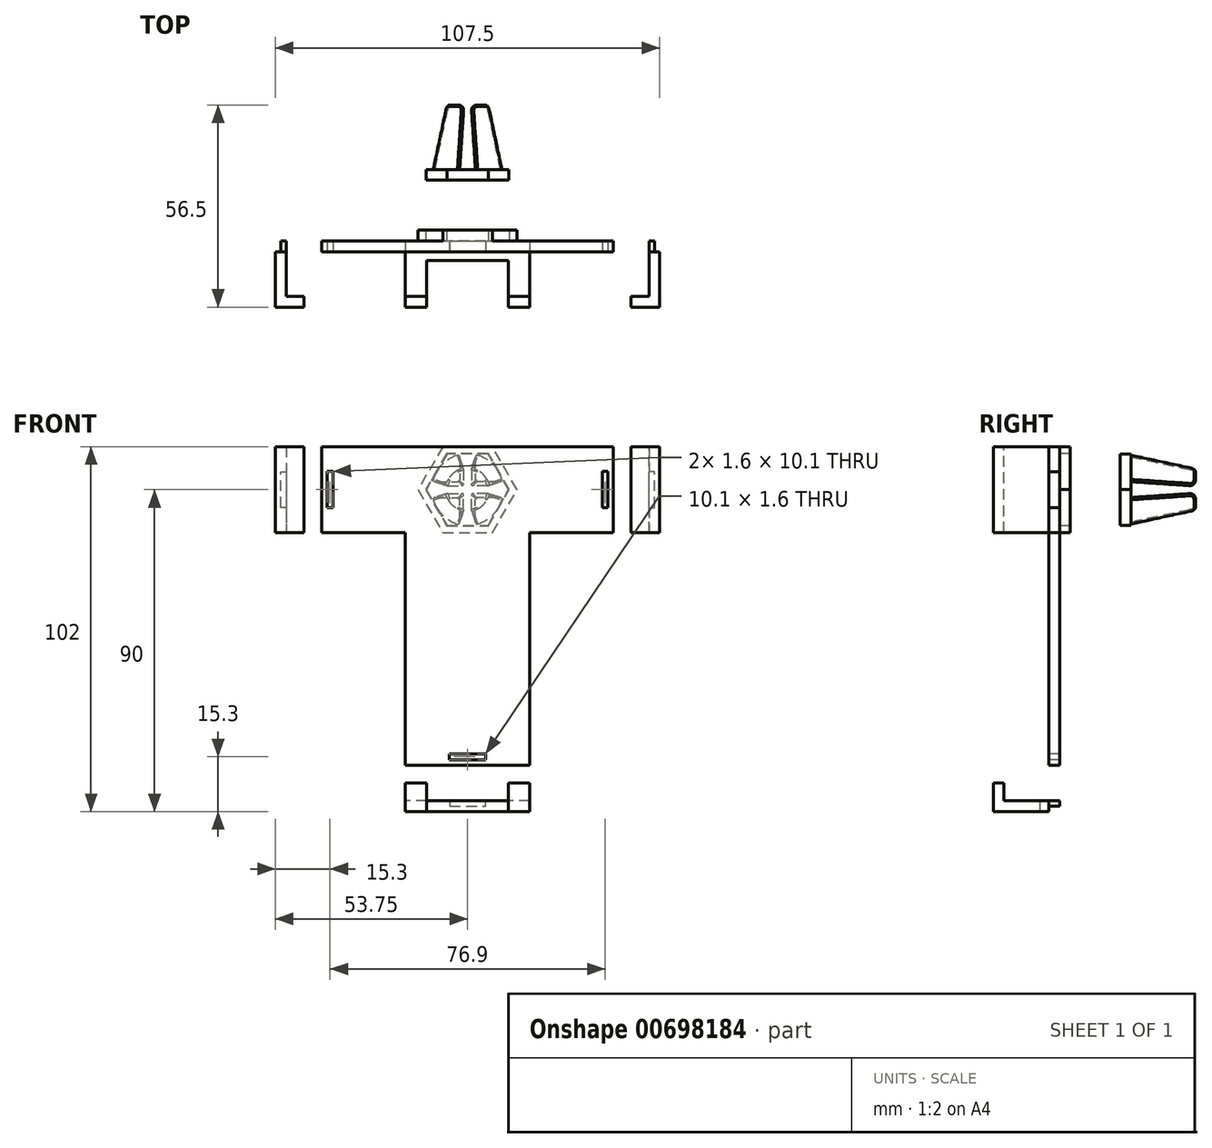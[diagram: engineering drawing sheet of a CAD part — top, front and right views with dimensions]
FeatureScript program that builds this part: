
annotation { "Feature Type Name" : "Feature", "Feature Type Description" : "" }
export const myFeature = defineFeature(function(context is Context, id is Id, definition is map)
    precondition{}
    {
        {
            assignVariable(context, id + "F0", {"name" : "depth_phone", "anyValue" : 12});
        }
        {
            var Q0;
            Q0=qCreatedBy(makeId("Front.planeOp"),FACE);
            var sketch = newSketch(context, id + "F1", { "sketchPlane" : qUnion([Q0])});
            skCircle(sketch, "E0", {"center": v(0, 0) * mm, "radius": 10 * mm});
            skSolve(sketch);
        }
        {
            var Q0;
            Q0=qSketchRegion(id+"F1",true);
            extrude(context, id + "F2", {"entities" : qUnion([Q0]), "oppositeDirection" : true, "depth" : 3 * mm});
        }
        {
            var Q0;
            Q0=makeQuery(id+"F2.opExtrude","CAP_FACE",FACE,{"disambiguationData":[OSD([sQuery(id+"F1.wireOp",EDGE,"E0")])],"isStart":false});
            var sketch = newSketch(context, id + "F3", { "sketchPlane" : qUnion([Q0])});
            skLineSegment(sketch, "E1.top", {"start": v(-9.75, 2.2) * mm, "end": v(-2.2, 2.2) * mm});
            skLineSegment(sketch, "E1.right", {"start": v(-2.2, 9.75) * mm, "end": v(-2.2, 2.2) * mm});
            skArc(sketch, "E2", {"start": v(-2.2, 9.75) * mm, "mid": v(-7.07, 7.07) * mm, "end": v(-9.75, 2.2) * mm});
            skLineSegment(sketch, "E3.1.0", {"start": v(-9.75, -2.2) * mm, "end": v(-2.2, -2.2) * mm});
            skLineSegment(sketch, "E3.1.1", {"start": v(-2.2, -9.75) * mm, "end": v(-2.2, -2.2) * mm});
            skArc(sketch, "E3.1.2", {"start": v(-9.75, -2.2) * mm, "mid": v(-7.07, -7.07) * mm, "end": v(-2.2, -9.75) * mm});
            skLineSegment(sketch, "E3.2.0", {"start": v(2.2, -9.75) * mm, "end": v(2.2, -2.2) * mm});
            skLineSegment(sketch, "E3.2.1", {"start": v(9.75, -2.2) * mm, "end": v(2.2, -2.2) * mm});
            skArc(sketch, "E3.2.2", {"start": v(2.2, -9.75) * mm, "mid": v(7.07, -7.07) * mm, "end": v(9.75, -2.2) * mm});
            skLineSegment(sketch, "E4.2.3.0", {"start": v(9.75, 2.2) * mm, "end": v(2.2, 2.2) * mm});
            skLineSegment(sketch, "E4.3.3.0", {"start": v(2.2, 9.75) * mm, "end": v(2.2, 2.2) * mm});
            skArc(sketch, "E4.6.3.0", {"start": v(9.75, 2.2) * mm, "mid": v(7.07, 7.07) * mm, "end": v(2.2, 9.75) * mm});
            skSolve(sketch);
        }
        {
            var Q0;
            Q0=makeQuery(id+"F3.imprint","IMPRINT",FACE,{"disambiguationData":[TD([[makeQuery(id+"F3.imprint","IMPRINT",EDGE,{"derivedFrom":sQuery(id+"F3.wireOp",EDGE,"E1.top")}),-1.0]])]});
            cPlane(context, id + "F4", {"entities" : qUnion([Q0]), "cplaneType" : CPlaneType.OFFSET, "offset" : 18 * mm, "width" : 150 * mm, "height" : 150 * mm});
        }
        {
            var Q0;
            Q0=qCreatedBy(id+"F4.planeOp",FACE);
            var sketch = newSketch(context, id + "F5", { "sketchPlane" : qUnion([Q0])});
            skLineSegment(sketch, "E5.top", {"start": v(-5.92, 1) * mm, "end": v(-1, 1) * mm});
            skLineSegment(sketch, "E5.right", {"start": v(-1, 5.92) * mm, "end": v(-1, 1) * mm});
            skArc(sketch, "E6", {"start": v(-1, 5.92) * mm, "mid": v(-4.24, 4.24) * mm, "end": v(-5.92, 1) * mm});
            skLineSegment(sketch, "E7.1.0", {"start": v(-5.92, -1) * mm, "end": v(-1, -1) * mm});
            skLineSegment(sketch, "E7.1.1", {"start": v(-1, -5.92) * mm, "end": v(-1, -1) * mm});
            skArc(sketch, "E7.1.2", {"start": v(-5.92, -1) * mm, "mid": v(-4.24, -4.24) * mm, "end": v(-1, -5.92) * mm});
            skLineSegment(sketch, "E7.2.0", {"start": v(1, -5.92) * mm, "end": v(1, -1) * mm});
            skLineSegment(sketch, "E7.2.1", {"start": v(5.92, -1) * mm, "end": v(1, -1) * mm});
            skArc(sketch, "E7.2.2", {"start": v(1, -5.92) * mm, "mid": v(4.24, -4.24) * mm, "end": v(5.92, -1) * mm});
            skLineSegment(sketch, "E7.3.0", {"start": v(5.92, 1) * mm, "end": v(1, 1) * mm});
            skLineSegment(sketch, "E7.3.1", {"start": v(1, 5.92) * mm, "end": v(1, 1) * mm});
            skArc(sketch, "E7.3.2", {"start": v(5.92, 1) * mm, "mid": v(4.24, 4.24) * mm, "end": v(1, 5.92) * mm});
            skSolve(sketch);
        }
        {
            var Q1;
            Q1=makeQuery(id+"F5.imprint","IMPRINT",FACE,{"disambiguationData":[TD([[makeQuery(id+"F5.imprint","IMPRINT",EDGE,{"derivedFrom":sQuery(id+"F5.wireOp",EDGE,"E5.top")}),1.0]])]});
            var Q2;
            Q2=makeQuery(id+"F3.imprint","IMPRINT",FACE,{"disambiguationData":[TD([[makeQuery(id+"F3.imprint","IMPRINT",EDGE,{"derivedFrom":sQuery(id+"F3.wireOp",EDGE,"E1.top")}),1.0]])]});
            loft(context, id + "F6", {"operationType" : NewBodyOperationType.ADD, "sheetProfilesArray" : [{ "sheetProfileEntities" : qUnion([Q1]) }, { "sheetProfileEntities" : qUnion([Q2]) }]});
        }
        {
            var Q1;
            Q1=makeQuery(id+"F3.imprint","IMPRINT",FACE,{"disambiguationData":[TD([[makeQuery(id+"F3.imprint","IMPRINT",EDGE,{"derivedFrom":sQuery(id+"F3.wireOp",EDGE,"E4.2.3.0")}),-1.0]])]});
            var Q2;
            Q2=makeQuery(id+"F5.imprint","IMPRINT",FACE,{"disambiguationData":[TD([[makeQuery(id+"F5.imprint","IMPRINT",EDGE,{"derivedFrom":sQuery(id+"F5.wireOp",EDGE,"E7.3.0")}),-1.0]])]});
            loft(context, id + "F7", {"operationType" : NewBodyOperationType.ADD, "sheetProfilesArray" : [{ "sheetProfileEntities" : qUnion([Q1]) }, { "sheetProfileEntities" : qUnion([Q2]) }]});
        }
        {
            var Q1;
            Q1=makeQuery(id+"F3.imprint","IMPRINT",FACE,{"disambiguationData":[TD([[makeQuery(id+"F3.imprint","IMPRINT",EDGE,{"derivedFrom":sQuery(id+"F3.wireOp",EDGE,"E3.1.0")}),-1.0]])]});
            var Q2;
            Q2=makeQuery(id+"F5.imprint","IMPRINT",FACE,{"disambiguationData":[TD([[makeQuery(id+"F5.imprint","IMPRINT",EDGE,{"derivedFrom":sQuery(id+"F5.wireOp",EDGE,"E7.1.0")}),-1.0]])]});
            loft(context, id + "F8", {"operationType" : NewBodyOperationType.ADD, "sheetProfilesArray" : [{ "sheetProfileEntities" : qUnion([Q1]) }, { "sheetProfileEntities" : qUnion([Q2]) }]});
        }
        {
            var Q1;
            Q1=makeQuery(id+"F3.imprint","IMPRINT",FACE,{"disambiguationData":[TD([[makeQuery(id+"F3.imprint","IMPRINT",EDGE,{"derivedFrom":sQuery(id+"F3.wireOp",EDGE,"E3.2.0")}),-1.0]])]});
            var Q2;
            Q2=makeQuery(id+"F5.imprint","IMPRINT",FACE,{"disambiguationData":[TD([[makeQuery(id+"F5.imprint","IMPRINT",EDGE,{"derivedFrom":sQuery(id+"F5.wireOp",EDGE,"E7.2.0")}),-1.0]])]});
            loft(context, id + "F9", {"operationType" : NewBodyOperationType.ADD, "sheetProfilesArray" : [{ "sheetProfileEntities" : qUnion([Q1]) }, { "sheetProfileEntities" : qUnion([Q2]) }]});
        }
        {
            var Q0;
            {var subQ0=sQuery(id+"F5.wireOp",EDGE,"E6");var subQ1=sQuery(id+"F5.wireOp",EDGE,"E5.right");var subQ2=sQuery(id+"F5.wireOp",EDGE,"E5.top");Q0=makeQuery(id+"F6.opLoft","MID_CAP_EDGE",EDGE,{"disambiguationData":[OSD([subQ2,subQ1,subQ0]),TDD([makeQuery(id+"F5.imprint","INTERSECT",VERTEX,{"derivedFrom":[subQ2,subQ0]}),makeQuery(id+"F5.imprint","INTERSECT",VERTEX,{"derivedFrom":[subQ1,subQ0]}),makeQuery(id+"F5.imprint","IMPRINT",EDGE,{"derivedFrom":subQ0})])],"capPos":0.0});}
            var Q1;
            Q1=makeQuery(id+"F6.opLoft","SWEPT_EDGE",EDGE,{"disambiguationData":[OSD([sQuery(id+"F3.wireOp",EDGE,"E1.right"),sQuery(id+"F3.wireOp",EDGE,"E2"),sQuery(id+"F5.wireOp",EDGE,"E5.right"),sQuery(id+"F5.wireOp",EDGE,"E6")])]});
            var Q2;
            Q2=makeQuery(id+"F6.opLoft","SWEPT_EDGE",EDGE,{"disambiguationData":[OSD([sQuery(id+"F3.wireOp",EDGE,"E1.top"),sQuery(id+"F3.wireOp",EDGE,"E1.right"),sQuery(id+"F5.wireOp",EDGE,"E5.top"),sQuery(id+"F5.wireOp",EDGE,"E5.right")])]});
            var Q3;
            Q3=makeQuery(id+"F6.opLoft","SWEPT_EDGE",EDGE,{"disambiguationData":[OSD([sQuery(id+"F3.wireOp",EDGE,"E1.top"),sQuery(id+"F3.wireOp",EDGE,"E2"),sQuery(id+"F5.wireOp",EDGE,"E5.top"),sQuery(id+"F5.wireOp",EDGE,"E6")])]});
            var Q4;
            {var subQ0=sQuery(id+"F5.wireOp",EDGE,"E7.1.2");var subQ1=sQuery(id+"F5.wireOp",EDGE,"E7.1.1");var subQ2=sQuery(id+"F5.wireOp",EDGE,"E7.1.0");Q4=makeQuery(id+"F8.opLoft","MID_CAP_EDGE",EDGE,{"disambiguationData":[OSD([subQ2,subQ1,subQ0]),TDD([makeQuery(id+"F5.imprint","INTERSECT",VERTEX,{"derivedFrom":[subQ2,subQ0]}),makeQuery(id+"F5.imprint","INTERSECT",VERTEX,{"derivedFrom":[subQ1,subQ0]}),makeQuery(id+"F5.imprint","IMPRINT",EDGE,{"derivedFrom":subQ0})])],"capPos":1.0});}
            var Q5;
            Q5=makeQuery(id+"F8.opLoft","SWEPT_EDGE",EDGE,{"disambiguationData":[OSD([sQuery(id+"F3.wireOp",EDGE,"E3.1.0"),sQuery(id+"F3.wireOp",EDGE,"E3.1.2"),sQuery(id+"F5.wireOp",EDGE,"E7.1.0"),sQuery(id+"F5.wireOp",EDGE,"E7.1.2")])]});
            var Q6;
            Q6=makeQuery(id+"F8.opLoft","SWEPT_EDGE",EDGE,{"disambiguationData":[OSD([sQuery(id+"F3.wireOp",EDGE,"E3.1.0"),sQuery(id+"F3.wireOp",EDGE,"E3.1.1"),sQuery(id+"F5.wireOp",EDGE,"E7.1.0"),sQuery(id+"F5.wireOp",EDGE,"E7.1.1")])]});
            var Q7;
            Q7=makeQuery(id+"F8.opLoft","SWEPT_EDGE",EDGE,{"disambiguationData":[OSD([sQuery(id+"F3.wireOp",EDGE,"E3.1.1"),sQuery(id+"F3.wireOp",EDGE,"E3.1.2"),sQuery(id+"F5.wireOp",EDGE,"E7.1.1"),sQuery(id+"F5.wireOp",EDGE,"E7.1.2")])]});
            var Q8;
            {var subQ0=sQuery(id+"F5.wireOp",EDGE,"E7.2.2");var subQ1=sQuery(id+"F5.wireOp",EDGE,"E7.2.1");var subQ2=sQuery(id+"F5.wireOp",EDGE,"E7.2.0");Q8=makeQuery(id+"F9.opLoft","MID_CAP_EDGE",EDGE,{"disambiguationData":[OSD([subQ2,subQ1,subQ0]),TDD([makeQuery(id+"F5.imprint","INTERSECT",VERTEX,{"derivedFrom":[subQ2,subQ0]}),makeQuery(id+"F5.imprint","INTERSECT",VERTEX,{"derivedFrom":[subQ1,subQ0]}),makeQuery(id+"F5.imprint","IMPRINT",EDGE,{"derivedFrom":subQ0})])],"capPos":1.0});}
            var Q9;
            Q9=makeQuery(id+"F9.opLoft","SWEPT_EDGE",EDGE,{"disambiguationData":[OSD([sQuery(id+"F3.wireOp",EDGE,"E3.2.0"),sQuery(id+"F3.wireOp",EDGE,"E3.2.2"),sQuery(id+"F5.wireOp",EDGE,"E7.2.0"),sQuery(id+"F5.wireOp",EDGE,"E7.2.2")])]});
            var Q10;
            Q10=makeQuery(id+"F9.opLoft","SWEPT_EDGE",EDGE,{"disambiguationData":[OSD([sQuery(id+"F3.wireOp",EDGE,"E3.2.1"),sQuery(id+"F3.wireOp",EDGE,"E3.2.2"),sQuery(id+"F5.wireOp",EDGE,"E7.2.1"),sQuery(id+"F5.wireOp",EDGE,"E7.2.2")])]});
            var Q11;
            Q11=makeQuery(id+"F9.opLoft","SWEPT_EDGE",EDGE,{"disambiguationData":[OSD([sQuery(id+"F3.wireOp",EDGE,"E3.2.0"),sQuery(id+"F3.wireOp",EDGE,"E3.2.1"),sQuery(id+"F5.wireOp",EDGE,"E7.2.0"),sQuery(id+"F5.wireOp",EDGE,"E7.2.1")])]});
            var Q12;
            {var subQ0=sQuery(id+"F5.wireOp",EDGE,"E7.3.2");var subQ1=sQuery(id+"F5.wireOp",EDGE,"E7.3.1");var subQ2=sQuery(id+"F5.wireOp",EDGE,"E7.3.0");Q12=makeQuery(id+"F7.opLoft","MID_CAP_EDGE",EDGE,{"disambiguationData":[OSD([subQ2,subQ1,subQ0]),TDD([makeQuery(id+"F5.imprint","INTERSECT",VERTEX,{"derivedFrom":[subQ2,subQ0]}),makeQuery(id+"F5.imprint","INTERSECT",VERTEX,{"derivedFrom":[subQ1,subQ0]}),makeQuery(id+"F5.imprint","IMPRINT",EDGE,{"derivedFrom":subQ0})])],"capPos":1.0});}
            var Q13;
            Q13=makeQuery(id+"F7.opLoft","SWEPT_EDGE",EDGE,{"disambiguationData":[OSD([sQuery(id+"F3.wireOp",EDGE,"E4.2.3.0"),sQuery(id+"F3.wireOp",EDGE,"E4.3.3.0"),sQuery(id+"F5.wireOp",EDGE,"E7.3.0"),sQuery(id+"F5.wireOp",EDGE,"E7.3.1")])]});
            var Q14;
            Q14=makeQuery(id+"F7.opLoft","SWEPT_EDGE",EDGE,{"disambiguationData":[OSD([sQuery(id+"F3.wireOp",EDGE,"E4.2.3.0"),sQuery(id+"F3.wireOp",EDGE,"E4.6.3.0"),sQuery(id+"F5.wireOp",EDGE,"E7.3.0"),sQuery(id+"F5.wireOp",EDGE,"E7.3.2")])]});
            var Q15;
            Q15=makeQuery(id+"F7.opLoft","SWEPT_EDGE",EDGE,{"disambiguationData":[OSD([sQuery(id+"F3.wireOp",EDGE,"E4.3.3.0"),sQuery(id+"F3.wireOp",EDGE,"E4.6.3.0"),sQuery(id+"F5.wireOp",EDGE,"E7.3.1"),sQuery(id+"F5.wireOp",EDGE,"E7.3.2")])]});
            fillet(context, id + "F10", {"entities" : qUnion([Q0, Q1, Q2, Q3, Q4, Q5, Q6, Q7, Q8, Q9, Q10, Q11, Q12, Q13, Q14, Q15]), "radius" : .5 * mm, "tangentPropagation" : true, "allowEdgeOverflow" : false});
        }
        {
            var Q0;
            Q0=qCreatedBy(makeId("Front.planeOp"),FACE);
            var sketch = newSketch(context, id + "F11", { "sketchPlane" : qUnion([Q0])});
            skLineSegment(sketch, "E8.bottom", {"start": v(86.03, 177.78) * mm, "end": v(32.03, 177.78) * mm});
            skLineSegment(sketch, "E8.top", {"start": v(86.03, 263.78) * mm, "end": v(32.03, 263.78) * mm});
            skLineSegment(sketch, "E8.left", {"start": v(86.03, 177.78) * mm, "end": v(86.03, 263.78) * mm});
            skLineSegment(sketch, "E8.right", {"start": v(32.03, 177.78) * mm, "end": v(32.03, 263.78) * mm});
            skSolve(sketch);
        }
        {
            var Q0;
            Q0=makeQuery(id+"F11.imprint","IMPRINT",FACE,{"disambiguationData":[TD([[makeQuery(id+"F11.imprint","IMPRINT",EDGE,{"derivedFrom":sQuery(id+"F11.wireOp",EDGE,"E8.bottom")}),-1.0]])]});
            extrude(context, id + "F12", {"entities" : qUnion([Q0]), "depth" : 1 * mm});
        }
        {
            var Q0;
            {var subQ0=sQuery(id+"F5.wireOp",EDGE,"E5.right");var subQ1=sQuery(id+"F5.wireOp",EDGE,"E6");var subQ2=sQuery(id+"F5.wireOp",EDGE,"E5.top");Q0=makeQuery(id+"F6.opLoft","MID_CAP_EDGE",EDGE,{"disambiguationData":[OSD([subQ2,subQ0,subQ1]),TDD([makeQuery(id+"F5.imprint","INTERSECT",VERTEX,{"derivedFrom":[subQ2,subQ0]}),makeQuery(id+"F5.imprint","INTERSECT",VERTEX,{"derivedFrom":[subQ0,subQ1]}),makeQuery(id+"F5.imprint","IMPRINT",EDGE,{"derivedFrom":subQ0})])],"capPos":0.0});}
            var Q1;
            {var subQ0=sQuery(id+"F5.wireOp",EDGE,"E5.top");var subQ1=sQuery(id+"F5.wireOp",EDGE,"E5.right");var subQ2=sQuery(id+"F5.wireOp",EDGE,"E6");Q1=makeQuery(id+"F6.opLoft","MID_CAP_EDGE",EDGE,{"disambiguationData":[OSD([subQ0,subQ1,subQ2]),TDD([makeQuery(id+"F5.imprint","INTERSECT",VERTEX,{"derivedFrom":[subQ0,subQ2]}),makeQuery(id+"F5.imprint","INTERSECT",VERTEX,{"derivedFrom":[subQ0,subQ1]}),makeQuery(id+"F5.imprint","IMPRINT",EDGE,{"derivedFrom":subQ0})])],"capPos":0.0});}
            var Q2;
            {var subQ0=sQuery(id+"F5.wireOp",EDGE,"E7.1.0");var subQ1=sQuery(id+"F5.wireOp",EDGE,"E7.1.1");var subQ2=sQuery(id+"F5.wireOp",EDGE,"E7.1.2");Q2=makeQuery(id+"F8.opLoft","MID_CAP_EDGE",EDGE,{"disambiguationData":[OSD([subQ0,subQ1,subQ2]),TDD([makeQuery(id+"F5.imprint","INTERSECT",VERTEX,{"derivedFrom":[subQ0,subQ2]}),makeQuery(id+"F5.imprint","INTERSECT",VERTEX,{"derivedFrom":[subQ0,subQ1]}),makeQuery(id+"F5.imprint","IMPRINT",EDGE,{"derivedFrom":subQ0})])],"capPos":1.0});}
            var Q3;
            {var subQ0=sQuery(id+"F5.wireOp",EDGE,"E7.1.1");var subQ1=sQuery(id+"F5.wireOp",EDGE,"E7.1.2");var subQ2=sQuery(id+"F5.wireOp",EDGE,"E7.1.0");Q3=makeQuery(id+"F8.opLoft","MID_CAP_EDGE",EDGE,{"disambiguationData":[OSD([subQ2,subQ0,subQ1]),TDD([makeQuery(id+"F5.imprint","INTERSECT",VERTEX,{"derivedFrom":[subQ2,subQ0]}),makeQuery(id+"F5.imprint","INTERSECT",VERTEX,{"derivedFrom":[subQ0,subQ1]}),makeQuery(id+"F5.imprint","IMPRINT",EDGE,{"derivedFrom":subQ0})])],"capPos":1.0});}
            var Q4;
            {var subQ0=sQuery(id+"F5.wireOp",EDGE,"E7.2.0");var subQ1=sQuery(id+"F5.wireOp",EDGE,"E7.2.1");var subQ2=sQuery(id+"F5.wireOp",EDGE,"E7.2.2");Q4=makeQuery(id+"F9.opLoft","MID_CAP_EDGE",EDGE,{"disambiguationData":[OSD([subQ0,subQ1,subQ2]),TDD([makeQuery(id+"F5.imprint","INTERSECT",VERTEX,{"derivedFrom":[subQ0,subQ2]}),makeQuery(id+"F5.imprint","INTERSECT",VERTEX,{"derivedFrom":[subQ0,subQ1]}),makeQuery(id+"F5.imprint","IMPRINT",EDGE,{"derivedFrom":subQ0})])],"capPos":1.0});}
            var Q5;
            {var subQ0=sQuery(id+"F5.wireOp",EDGE,"E7.2.1");var subQ1=sQuery(id+"F5.wireOp",EDGE,"E7.2.2");var subQ2=sQuery(id+"F5.wireOp",EDGE,"E7.2.0");Q5=makeQuery(id+"F9.opLoft","MID_CAP_EDGE",EDGE,{"disambiguationData":[OSD([subQ2,subQ0,subQ1]),TDD([makeQuery(id+"F5.imprint","INTERSECT",VERTEX,{"derivedFrom":[subQ2,subQ0]}),makeQuery(id+"F5.imprint","INTERSECT",VERTEX,{"derivedFrom":[subQ0,subQ1]}),makeQuery(id+"F5.imprint","IMPRINT",EDGE,{"derivedFrom":subQ0})])],"capPos":1.0});}
            var Q6;
            {var subQ0=sQuery(id+"F5.wireOp",EDGE,"E7.3.0");var subQ1=sQuery(id+"F5.wireOp",EDGE,"E7.3.1");var subQ2=sQuery(id+"F5.wireOp",EDGE,"E7.3.2");Q6=makeQuery(id+"F7.opLoft","MID_CAP_EDGE",EDGE,{"disambiguationData":[OSD([subQ0,subQ1,subQ2]),TDD([makeQuery(id+"F5.imprint","INTERSECT",VERTEX,{"derivedFrom":[subQ0,subQ2]}),makeQuery(id+"F5.imprint","INTERSECT",VERTEX,{"derivedFrom":[subQ0,subQ1]}),makeQuery(id+"F5.imprint","IMPRINT",EDGE,{"derivedFrom":subQ0})])],"capPos":1.0});}
            var Q7;
            {var subQ0=sQuery(id+"F5.wireOp",EDGE,"E7.3.1");var subQ1=sQuery(id+"F5.wireOp",EDGE,"E7.3.2");var subQ2=sQuery(id+"F5.wireOp",EDGE,"E7.3.0");Q7=makeQuery(id+"F7.opLoft","MID_CAP_EDGE",EDGE,{"disambiguationData":[OSD([subQ2,subQ0,subQ1]),TDD([makeQuery(id+"F5.imprint","INTERSECT",VERTEX,{"derivedFrom":[subQ2,subQ0]}),makeQuery(id+"F5.imprint","INTERSECT",VERTEX,{"derivedFrom":[subQ0,subQ1]}),makeQuery(id+"F5.imprint","IMPRINT",EDGE,{"derivedFrom":subQ0})])],"capPos":1.0});}
            fillet(context, id + "F13", {"entities" : qUnion([Q0, Q1, Q2, Q3, Q4, Q5, Q6, Q7]), "radius" : 1.5 * mm, "tangentPropagation" : true, "allowEdgeOverflow" : false});
        }
        {
            var Q0;
            Q0=qCreatedBy(makeId("Front.planeOp"),FACE);
            var sketch = newSketch(context, id + "F14", { "sketchPlane" : qUnion([Q0])});
            skLineSegment(sketch, "E9.bottom", {"start": v(102.82, 40.15) * mm, "end": v(177.82, 40.15) * mm});
            skLineSegment(sketch, "E9.top", {"start": v(102.82, -107.85) * mm, "end": v(177.82, -107.85) * mm});
            skLineSegment(sketch, "E9.left", {"start": v(102.82, 40.15) * mm, "end": v(102.82, -107.85) * mm});
            skLineSegment(sketch, "E9.right", {"start": v(177.82, 40.15) * mm, "end": v(177.82, -107.85) * mm});
            skSolve(sketch);
        }
        {
            var Q0;
            Q0=qSketchRegion(id+"F14",true);
            extrude(context, id + "F15", {"entities" : qUnion([Q0]), "depth" : (getVariable(context, 'depth_phone')) * mm});
        }
        {
            var Q0;
            Q0=makeQuery(id+"F15.opExtrude","SWEPT_EDGE",EDGE,{"disambiguationData":[OSD([sQuery(id+"F14.wireOp",EDGE,"E9.bottom"),sQuery(id+"F14.wireOp",EDGE,"E9.left")])]});
            var Q1;
            Q1=makeQuery(id+"F15.opExtrude","SWEPT_EDGE",EDGE,{"disambiguationData":[OSD([sQuery(id+"F14.wireOp",EDGE,"E9.bottom"),sQuery(id+"F14.wireOp",EDGE,"E9.right")])]});
            var Q2;
            Q2=makeQuery(id+"F15.opExtrude","SWEPT_EDGE",EDGE,{"disambiguationData":[OSD([sQuery(id+"F14.wireOp",EDGE,"E9.top"),sQuery(id+"F14.wireOp",EDGE,"E9.right")])]});
            var Q3;
            Q3=makeQuery(id+"F15.opExtrude","SWEPT_EDGE",EDGE,{"disambiguationData":[OSD([sQuery(id+"F14.wireOp",EDGE,"E9.top"),sQuery(id+"F14.wireOp",EDGE,"E9.left")])]});
            fillet(context, id + "F16", {"entities" : qUnion([Q0, Q1, Q2, Q3]), "radius" : 2.5 * mm, "tangentPropagation" : true, "allowEdgeOverflow" : false});
        }
        {
            var Q0;
            Q0=makeQuery(id+"F15.opExtrude","CAP_EDGE",EDGE,{"disambiguationData":[OSD([sQuery(id+"F14.wireOp",EDGE,"E9.right")])],"isStart":true});
            var Q1;
            Q1=makeQuery(id+"F15.opExtrude","CAP_EDGE",EDGE,{"disambiguationData":[OSD([sQuery(id+"F14.wireOp",EDGE,"E9.bottom")])],"isStart":true});
            var Q2;
            Q2=makeQuery(id+"F15.opExtrude","CAP_EDGE",EDGE,{"disambiguationData":[OSD([sQuery(id+"F14.wireOp",EDGE,"E9.left")])],"isStart":true});
            var Q3;
            Q3=makeQuery(id+"F15.opExtrude","CAP_EDGE",EDGE,{"disambiguationData":[OSD([sQuery(id+"F14.wireOp",EDGE,"E9.top")])],"isStart":true});
            fillet(context, id + "F17", {"entities" : qUnion([Q0, Q1, Q2, Q3]), "radius" : 2.5 * mm, "tangentPropagation" : true, "allowEdgeOverflow" : false});
        }
        {
            var Q0;
            Q0=makeQuery(id+"F15.opExtrude","CAP_EDGE",EDGE,{"disambiguationData":[OSD([sQuery(id+"F14.wireOp",EDGE,"E9.right")])],"isStart":false});
            var Q1;
            Q1=makeQuery(id+"F15.opExtrude","CAP_EDGE",EDGE,{"disambiguationData":[OSD([sQuery(id+"F14.wireOp",EDGE,"E9.bottom")])],"isStart":false});
            var Q2;
            Q2=makeQuery(id+"F15.opExtrude","CAP_EDGE",EDGE,{"disambiguationData":[OSD([sQuery(id+"F14.wireOp",EDGE,"E9.left")])],"isStart":false});
            var Q3;
            Q3=makeQuery(id+"F15.opExtrude","CAP_EDGE",EDGE,{"disambiguationData":[OSD([sQuery(id+"F14.wireOp",EDGE,"E9.top")])],"isStart":false});
            fillet(context, id + "F18", {"entities" : qUnion([Q0, Q1, Q2, Q3]), "radius" : 12 * mm, "tangentPropagation" : true, "allowEdgeOverflow" : false});
        }
        {
            var Q0;
            Q0=qCreatedBy(makeId("Front.planeOp"),FACE);
            cPlane(context, id + "F19", {"entities" : qUnion([Q0]), "cplaneType" : CPlaneType.OFFSET, "offset" : 20 * mm, "width" : 150 * mm, "height" : 150 * mm});
        }
        {
            var Q0;
            Q0=qCreatedBy(id+"F19.planeOp",FACE);
            var sketch = newSketch(context, id + "F20", { "sketchPlane" : qUnion([Q0])});
            skLineSegment(sketch, "E10.bottom", {"start": v(-17.4, -77) * mm, "end": v(17.4, -77) * mm});
            skLineSegment(sketch, "E10.top", {"start": v(-17.4, 0) * mm, "end": v(17.4, 0) * mm});
            skLineSegment(sketch, "E10.left", {"start": v(-17.4, -77) * mm, "end": v(-17.4, 0) * mm});
            skLineSegment(sketch, "E10.right", {"start": v(17.4, -77) * mm, "end": v(17.4, 0) * mm});
            skSolve(sketch);
        }
        {
            var Q0;
            Q0=qSketchRegion(id+"F20",true);
            extrude(context, id + "F21", {"entities" : qUnion([Q0]), "operationType" : NewBodyOperationType.ADD, "oppositeDirection" : true, "depth" : 3 * mm});
        }
        {
            var Q0;
            Q0=makeQuery(id+"F21.opExtrude","SWEPT_FACE",FACE,{"disambiguationData":[OSD([sQuery(id+"F20.wireOp",EDGE,"E10.bottom")])]});
            cPlane(context, id + "F22", {"entities" : qUnion([Q0]), "cplaneType" : CPlaneType.OFFSET, "offset" : 10 * mm, "width" : 150 * mm, "height" : 150 * mm});
        }
        {
            var Q0;
            Q0=qCreatedBy(id+"F22.planeOp",FACE);
            var sketch = newSketch(context, id + "F23", { "sketchPlane" : qUnion([Q0])});
            skLineSegment(sketch, "E11.bottom", {"start": v(17.4, 17) * mm, "end": v(-17.4, 17) * mm});
            skLineSegment(sketch, "E11.top", {"start": v(17.4, 32.5) * mm, "end": v(-17.4, 32.5) * mm});
            skLineSegment(sketch, "E11.left", {"start": v(17.4, 17) * mm, "end": v(17.4, 32.5) * mm});
            skLineSegment(sketch, "E11.right", {"start": v(-17.4, 17) * mm, "end": v(-17.4, 32.5) * mm});
            skSolve(sketch);
        }
        {
            var Q0;
            Q0=qSketchRegion(id+"F23",true);
            extrude(context, id + "F24", {"entities" : qUnion([Q0]), "operationType" : NewBodyOperationType.ADD, "depth" : 3 * mm});
        }
        {
            var Q0;
            Q0=qCreatedBy(id+"F19.planeOp",FACE);
            var sketch = newSketch(context, id + "F25", { "sketchPlane" : qUnion([Q0])});
            skLineSegment(sketch, "E12.bottom", {"start": v(40.75, 12) * mm, "end": v(-40.75, 12) * mm});
            skLineSegment(sketch, "E12.top", {"start": v(40.75, -12) * mm, "end": v(-40.75, -12) * mm});
            skLineSegment(sketch, "E12.left", {"start": v(40.75, 12) * mm, "end": v(40.75, -12) * mm});
            skLineSegment(sketch, "E12.right", {"start": v(-40.75, 12) * mm, "end": v(-40.75, -12) * mm});
            skLineSegment(sketch, "E13", {"start": v(40.75, 0) * mm, "end": v(-40.75, 0) * mm, "construction": true});
            skLineSegment(sketch, "E14", {"start": v(0, -12) * mm, "end": v(0, 12) * mm, "construction": true});
            skPoint(sketch, "E15", {"position": v(0, 0) * mm});
            skSolve(sketch);
        }
        {
            var Q0;
            Q0=makeQuery(id+"F25.imprint","IMPRINT",FACE,{"disambiguationData":[TD([[makeQuery(id+"F25.imprint","IMPRINT",EDGE,{"derivedFrom":sQuery(id+"F25.wireOp",EDGE,"E12.bottom")}),1.0]])]});
            extrude(context, id + "F26", {"entities" : qUnion([Q0]), "operationType" : NewBodyOperationType.ADD, "oppositeDirection" : true, "depth" : 3 * mm});
        }
        {
            var Q0;
            Q0=makeQuery(id+"F26.opExtrude","SWEPT_FACE",FACE,{"disambiguationData":[OSD([sQuery(id+"F25.wireOp",EDGE,"E12.right")])]});
            cPlane(context, id + "F27", {"entities" : qUnion([Q0]), "cplaneType" : CPlaneType.OFFSET, "offset" : 10 * mm, "width" : 150 * mm, "height" : 150 * mm});
        }
        {
            var Q0;
            Q0=qCreatedBy(id+"F27.planeOp",FACE);
            var sketch = newSketch(context, id + "F28", { "sketchPlane" : qUnion([Q0])});
            skLineSegment(sketch, "E16.bottom", {"start": v(17, 12) * mm, "end": v(32.5, 12) * mm});
            skLineSegment(sketch, "E16.top", {"start": v(17, -12) * mm, "end": v(32.5, -12) * mm});
            skLineSegment(sketch, "E16.left", {"start": v(17, 12) * mm, "end": v(17, -12) * mm});
            skLineSegment(sketch, "E16.right", {"start": v(32.5, 12) * mm, "end": v(32.5, -12) * mm});
            skSolve(sketch);
        }
        {
            var Q0;
            Q0=qSketchRegion(id+"F28",true);
            extrude(context, id + "F29", {"entities" : qUnion([Q0]), "operationType" : NewBodyOperationType.ADD, "depth" : 3 * mm});
        }
        {
            var Q0;
            Q0=makeQuery(id+"F26.opExtrude","SWEPT_FACE",FACE,{"disambiguationData":[OSD([sQuery(id+"F25.wireOp",EDGE,"E12.left")])]});
            cPlane(context, id + "F30", {"entities" : qUnion([Q0]), "cplaneType" : CPlaneType.OFFSET, "offset" : 10 * mm, "width" : 150 * mm, "height" : 150 * mm});
        }
        {
            var Q0;
            Q0=qCreatedBy(id+"F30.planeOp",FACE);
            var sketch = newSketch(context, id + "F31", { "sketchPlane" : qUnion([Q0])});
            skLineSegment(sketch, "E17.bottom", {"start": v(-17, -12) * mm, "end": v(-32.5, -12) * mm});
            skLineSegment(sketch, "E17.top", {"start": v(-17, 12) * mm, "end": v(-32.5, 12) * mm});
            skLineSegment(sketch, "E17.left", {"start": v(-17, -12) * mm, "end": v(-17, 12) * mm});
            skLineSegment(sketch, "E17.right", {"start": v(-32.5, -12) * mm, "end": v(-32.5, 12) * mm});
            skSolve(sketch);
        }
        {
            var Q0;
            Q0=qSketchRegion(id+"F31",true);
            extrude(context, id + "F32", {"entities" : qUnion([Q0]), "operationType" : NewBodyOperationType.ADD, "depth" : 3 * mm});
        }
        {
            var Q0;
            Q0=makeQuery(id+"F24.opExtrude","CAP_FACE",FACE,{"disambiguationData":[OSD([sQuery(id+"F23.wireOp",EDGE,"E11.bottom"),sQuery(id+"F23.wireOp",EDGE,"E11.top"),sQuery(id+"F23.wireOp",EDGE,"E11.left"),sQuery(id+"F23.wireOp",EDGE,"E11.right")])],"isStart":false});
            var sketch = newSketch(context, id + "F33", { "sketchPlane" : qUnion([Q0])});
            skLineSegment(sketch, "E18.bottom", {"start": v(-11.4, 32.5) * mm, "end": v(11.4, 32.5) * mm});
            skLineSegment(sketch, "E18.top", {"start": v(-11.4, 20) * mm, "end": v(11.4, 20) * mm});
            skLineSegment(sketch, "E18.left", {"start": v(-11.4, 32.5) * mm, "end": v(-11.4, 20) * mm});
            skLineSegment(sketch, "E18.right", {"start": v(11.4, 32.5) * mm, "end": v(11.4, 20) * mm});
            skLineSegment(sketch, "E19", {"start": v(0, 20) * mm, "end": v(0, 32.5) * mm, "construction": true});
            skSolve(sketch);
        }
        {
            var Q0;
            Q0=qSketchRegion(id+"F33",true);
            extrude(context, id + "F34", {"entities" : qUnion([Q0]), "operationType" : NewBodyOperationType.REMOVE, "endBound" : BoundingType.UP_TO_NEXT, "oppositeDirection" : true, "depth" : 25 * mm});
        }
        {
            var Q0;
            Q0=makeQuery(id+"F29.opExtrude","SWEPT_FACE",FACE,{"disambiguationData":[OSD([sQuery(id+"F28.wireOp",EDGE,"E16.right")])]});
            var sketch = newSketch(context, id + "F35", { "sketchPlane" : qUnion([Q0])});
            skLineSegment(sketch, "E20.bottom", {"start": v(-53.75, -12) * mm, "end": v(-45.75, -12) * mm});
            skLineSegment(sketch, "E20.top", {"start": v(-53.75, 12) * mm, "end": v(-45.75, 12) * mm});
            skLineSegment(sketch, "E20.left", {"start": v(-53.75, -12) * mm, "end": v(-53.75, 12) * mm});
            skLineSegment(sketch, "E20.right", {"start": v(-45.75, -12) * mm, "end": v(-45.75, 12) * mm});
            skLineSegment(sketch, "E21.bottom", {"start": v(53.75, -12) * mm, "end": v(45.75, -12) * mm});
            skLineSegment(sketch, "E21.top", {"start": v(53.75, 12) * mm, "end": v(45.75, 12) * mm});
            skLineSegment(sketch, "E21.left", {"start": v(53.75, -12) * mm, "end": v(53.75, 12) * mm});
            skLineSegment(sketch, "E21.right", {"start": v(45.75, -12) * mm, "end": v(45.75, 12) * mm});
            skLineSegment(sketch, "E22.bottom", {"start": v(-17.4, -90) * mm, "end": v(-11.4, -90) * mm});
            skLineSegment(sketch, "E22.top", {"start": v(-17.4, -82) * mm, "end": v(-11.4, -82) * mm});
            skLineSegment(sketch, "E22.left", {"start": v(-17.4, -90) * mm, "end": v(-17.4, -82) * mm});
            skLineSegment(sketch, "E22.right", {"start": v(-11.4, -90) * mm, "end": v(-11.4, -82) * mm});
            skLineSegment(sketch, "E23.bottom", {"start": v(11.4, -90) * mm, "end": v(17.4, -90) * mm});
            skLineSegment(sketch, "E23.top", {"start": v(11.4, -82) * mm, "end": v(17.4, -82) * mm});
            skLineSegment(sketch, "E23.left", {"start": v(11.4, -90) * mm, "end": v(11.4, -82) * mm});
            skLineSegment(sketch, "E23.right", {"start": v(17.4, -90) * mm, "end": v(17.4, -82) * mm});
            skSolve(sketch);
        }
        {
            var Q0;
            Q0=qSketchRegion(id+"F35",true);
            extrude(context, id + "F36", {"entities" : qUnion([Q0]), "operationType" : NewBodyOperationType.ADD, "depth" : 3 * mm});
        }
        {
            var Q0;
            Q0=makeQuery(id+"F32.boolean.opBoolean","MERGE",FACE,{"derivedFrom":[makeQuery(id+"F29.boolean.opBoolean","MERGE",FACE,{"derivedFrom":[makeQuery(id+"F26.boolean.opBoolean","MERGE",FACE,{"derivedFrom":[makeQuery(id+"F24.boolean.opBoolean","MERGE",FACE,{"derivedFrom":[makeQuery(id+"F21.opExtrude","CAP_FACE",FACE,{"disambiguationData":[OSD([sQuery(id+"F20.wireOp",EDGE,"E10.bottom"),sQuery(id+"F20.wireOp",EDGE,"E10.top"),sQuery(id+"F20.wireOp",EDGE,"E10.left"),sQuery(id+"F20.wireOp",EDGE,"E10.right")])],"isStart":false}),makeQuery(id+"F24.opExtrude","SWEPT_FACE",FACE,{"disambiguationData":[OSD([sQuery(id+"F23.wireOp",EDGE,"E11.bottom")])]})]}),makeQuery(id+"F26.opExtrude","CAP_FACE",FACE,{"disambiguationData":[OSD([sQuery(id+"F25.wireOp",EDGE,"E12.bottom"),sQuery(id+"F25.wireOp",EDGE,"E12.top"),sQuery(id+"F25.wireOp",EDGE,"E12.left"),sQuery(id+"F25.wireOp",EDGE,"E12.right")])],"isStart":false})]}),makeQuery(id+"F29.opExtrude","SWEPT_FACE",FACE,{"disambiguationData":[OSD([sQuery(id+"F28.wireOp",EDGE,"E16.left")])]})]}),makeQuery(id+"F32.opExtrude","SWEPT_FACE",FACE,{"disambiguationData":[OSD([sQuery(id+"F31.wireOp",EDGE,"E17.left")])]})]});
            var sketch = newSketch(context, id + "F37", { "sketchPlane" : qUnion([Q0])});
            skCircle(sketch, "E24.cCircle", {"center": v(0, 0) * mm, "radius": 10.1 * mm, "construction": true});
            skLineSegment(sketch, "E24.0", {"start": v(11.66, 0) * mm, "end": v(5.83, -10.1) * mm});
            skLineSegment(sketch, "E24.1", {"start": v(5.83, -10.1) * mm, "end": v(-5.83, -10.1) * mm});
            skLineSegment(sketch, "E24.2", {"start": v(-5.83, -10.1) * mm, "end": v(-11.66, 0) * mm});
            skLineSegment(sketch, "E24.3", {"start": v(-11.66, 0) * mm, "end": v(-5.83, 10.1) * mm});
            skLineSegment(sketch, "E24.4", {"start": v(-5.83, 10.1) * mm, "end": v(5.83, 10.1) * mm});
            skLineSegment(sketch, "E24.5", {"start": v(5.83, 10.1) * mm, "end": v(11.66, 0) * mm});
            skPoint(sketch, "E24.0.midPoint", {"position": v(8.75, -5.05) * mm});
            skCircle(sketch, "E25.cCircle", {"center": v(0, 0) * mm, "radius": 12 * mm, "construction": true});
            skLineSegment(sketch, "E25.0", {"start": v(13.86, 0) * mm, "end": v(6.93, -12) * mm});
            skLineSegment(sketch, "E25.1", {"start": v(6.93, -12) * mm, "end": v(-6.93, -12) * mm});
            skLineSegment(sketch, "E25.2", {"start": v(-6.93, -12) * mm, "end": v(-13.86, 0) * mm});
            skLineSegment(sketch, "E25.3", {"start": v(-13.86, 0) * mm, "end": v(-6.93, 12) * mm});
            skLineSegment(sketch, "E25.4", {"start": v(-6.93, 12) * mm, "end": v(6.93, 12) * mm});
            skLineSegment(sketch, "E25.5", {"start": v(6.93, 12) * mm, "end": v(13.86, 0) * mm});
            skPoint(sketch, "E25.0.midPoint", {"position": v(10.4, -6) * mm});
            skSolve(sketch);
        }
        {
            var Q0;
            Q0=qSketchRegion(id+"F37",true);
            extrude(context, id + "F38", {"entities" : qUnion([Q0]), "operationType" : NewBodyOperationType.ADD, "depth" : 3 * mm});
        }
        {
            var Q0;
            Q0=makeQuery(id+"F2.opExtrude","CAP_FACE",FACE,{"disambiguationData":[OSD([sQuery(id+"F1.wireOp",EDGE,"E0")])],"isStart":false});
            var sketch = newSketch(context, id + "F39", { "sketchPlane" : qUnion([Q0])});
            skCircle(sketch, "E26.cCircle", {"center": v(0, 0) * mm, "radius": 10 * mm, "construction": true});
            skLineSegment(sketch, "E26.0", {"start": v(11.55, 0) * mm, "end": v(5.77, -10) * mm});
            skLineSegment(sketch, "E26.1", {"start": v(5.77, -10) * mm, "end": v(-5.77, -10) * mm});
            skLineSegment(sketch, "E26.2", {"start": v(-5.77, -10) * mm, "end": v(-11.55, 0) * mm});
            skLineSegment(sketch, "E26.3", {"start": v(-11.55, 0) * mm, "end": v(-5.77, 10) * mm});
            skLineSegment(sketch, "E26.4", {"start": v(-5.77, 10) * mm, "end": v(5.77, 10) * mm});
            skLineSegment(sketch, "E26.5", {"start": v(5.77, 10) * mm, "end": v(11.55, 0) * mm});
            skPoint(sketch, "E26.0.midPoint", {"position": v(8.66, -5) * mm});
            skSolve(sketch);
        }
        {
            var Q0;
            Q0=qSketchRegion(id+"F39",true);
            extrude(context, id + "F40", {"entities" : qUnion([Q0]), "operationType" : NewBodyOperationType.ADD, "oppositeDirection" : true, "depth" : 3 * mm});
        }
        {
            var Q0;
            Q0=makeQuery(id+"F26.boolean.opBoolean","MERGE",FACE,{"derivedFrom":[makeQuery(id+"F21.opExtrude","CAP_FACE",FACE,{"disambiguationData":[OSD([sQuery(id+"F20.wireOp",EDGE,"E10.bottom"),sQuery(id+"F20.wireOp",EDGE,"E10.top"),sQuery(id+"F20.wireOp",EDGE,"E10.left"),sQuery(id+"F20.wireOp",EDGE,"E10.right")])],"isStart":true}),makeQuery(id+"F26.opExtrude","CAP_FACE",FACE,{"disambiguationData":[OSD([sQuery(id+"F25.wireOp",EDGE,"E12.bottom"),sQuery(id+"F25.wireOp",EDGE,"E12.top"),sQuery(id+"F25.wireOp",EDGE,"E12.left"),sQuery(id+"F25.wireOp",EDGE,"E12.right")])],"isStart":true})]});
            var sketch = newSketch(context, id + "F41", { "sketchPlane" : qUnion([Q0])});
            skLineSegment(sketch, "E27.bottom", {"start": v(-39.25, 5.05) * mm, "end": v(-37.65, 5.05) * mm});
            skLineSegment(sketch, "E27.top", {"start": v(-39.25, -5.05) * mm, "end": v(-37.65, -5.05) * mm});
            skLineSegment(sketch, "E27.left", {"start": v(-39.25, 5.05) * mm, "end": v(-39.25, -5.05) * mm});
            skLineSegment(sketch, "E27.right", {"start": v(-37.65, 5.05) * mm, "end": v(-37.65, -5.05) * mm});
            skLineSegment(sketch, "E28", {"start": v(-39.25, 0) * mm, "end": v(-37.65, 0) * mm, "construction": true});
            skLineSegment(sketch, "E29", {"start": v(0, 8.73) * mm, "end": v(0, 0) * mm, "construction": true});
            skLineSegment(sketch, "E30.MirrorCS", {"start": v(37.65, 5.05) * mm, "end": v(37.65, -5.05) * mm});
            skLineSegment(sketch, "E31.MirrorCS", {"start": v(39.25, -5.05) * mm, "end": v(37.65, -5.05) * mm});
            skLineSegment(sketch, "E32.MirrorCS", {"start": v(39.25, 5.05) * mm, "end": v(39.25, -5.05) * mm});
            skLineSegment(sketch, "E33.MirrorCS", {"start": v(39.25, 5.05) * mm, "end": v(37.65, 5.05) * mm});
            skLineSegment(sketch, "E34.bottom", {"start": v(-5.05, -75.5) * mm, "end": v(5.05, -75.5) * mm});
            skLineSegment(sketch, "E34.top", {"start": v(-5.05, -73.9) * mm, "end": v(5.05, -73.9) * mm});
            skLineSegment(sketch, "E34.left", {"start": v(-5.05, -75.5) * mm, "end": v(-5.05, -73.9) * mm});
            skLineSegment(sketch, "E34.right", {"start": v(5.05, -75.5) * mm, "end": v(5.05, -73.9) * mm});
            skLineSegment(sketch, "E35", {"start": v(0, -73.9) * mm, "end": v(0, -75.5) * mm, "construction": true});
            skSolve(sketch);
        }
        {
            var Q0;
            Q0=qSketchRegion(id+"F41",true);
            extrude(context, id + "F42", {"entities" : qUnion([Q0]), "operationType" : NewBodyOperationType.REMOVE, "endBound" : BoundingType.UP_TO_NEXT, "oppositeDirection" : true, "depth" : 25 * mm});
        }
        {
            var Q0;
            Q0=qCreatedBy(id+"F19.planeOp",FACE);
            var sketch = newSketch(context, id + "F43", { "sketchPlane" : qUnion([Q0])});
            skLineSegment(sketch, "E36", {"start": v(53.75, -12) * mm, "end": v(53.75, 12) * mm});
            skLineSegment(sketch, "E37", {"start": v(53.75, 12) * mm, "end": v(50.75, 12) * mm});
            skLineSegment(sketch, "E38", {"start": v(50.75, 12) * mm, "end": v(50.75, 5) * mm});
            skLineSegment(sketch, "E39", {"start": v(50.75, 5) * mm, "end": v(52.25, 5) * mm});
            skLineSegment(sketch, "E40", {"start": v(52.25, 5) * mm, "end": v(52.25, -5) * mm});
            skLineSegment(sketch, "E41", {"start": v(52.25, -5) * mm, "end": v(50.75, -5) * mm});
            skLineSegment(sketch, "E42", {"start": v(50.75, -5) * mm, "end": v(50.75, -12) * mm});
            skLineSegment(sketch, "E43", {"start": v(50.75, -12) * mm, "end": v(53.75, -12) * mm});
            skLineSegment(sketch, "E44", {"start": v(52.25, 0) * mm, "end": v(40.9, 0) * mm, "construction": true});
            skLineSegment(sketch, "E45", {"start": v(0, 0) * mm, "end": v(0, -18) * mm, "construction": true});
            skLineSegment(sketch, "E46.MirrorCS", {"start": v(-53.75, -12) * mm, "end": v(-53.75, 12) * mm});
            skLineSegment(sketch, "E47.MirrorCS", {"start": v(-53.75, 12) * mm, "end": v(-50.75, 12) * mm});
            skLineSegment(sketch, "E48.MirrorCS", {"start": v(-50.75, 12) * mm, "end": v(-50.75, 5) * mm});
            skLineSegment(sketch, "E49.MirrorCS", {"start": v(-50.75, 5) * mm, "end": v(-52.25, 5) * mm});
            skLineSegment(sketch, "E50.MirrorCS", {"start": v(-52.25, 5) * mm, "end": v(-52.25, -5) * mm});
            skLineSegment(sketch, "E51.MirrorCS", {"start": v(-52.25, -5) * mm, "end": v(-50.75, -5) * mm});
            skLineSegment(sketch, "E52.MirrorCS", {"start": v(-50.75, -5) * mm, "end": v(-50.75, -12) * mm});
            skLineSegment(sketch, "E53.MirrorCS", {"start": v(-50.75, -12) * mm, "end": v(-53.75, -12) * mm});
            skLineSegment(sketch, "E54", {"start": v(17.4, -90) * mm, "end": v(-17.4, -90) * mm});
            skLineSegment(sketch, "E55", {"start": v(-17.4, -90) * mm, "end": v(-17.4, -87) * mm});
            skLineSegment(sketch, "E56", {"start": v(-17.4, -87) * mm, "end": v(-5, -87) * mm});
            skLineSegment(sketch, "E57", {"start": v(-5, -87) * mm, "end": v(-5, -88.5) * mm});
            skLineSegment(sketch, "E58", {"start": v(-5, -88.5) * mm, "end": v(5, -88.5) * mm});
            skLineSegment(sketch, "E59", {"start": v(5, -88.5) * mm, "end": v(5, -87) * mm});
            skLineSegment(sketch, "E60", {"start": v(5, -87) * mm, "end": v(17.4, -87) * mm});
            skLineSegment(sketch, "E61", {"start": v(17.4, -87) * mm, "end": v(17.4, -90) * mm});
            skLineSegment(sketch, "E62", {"start": v(0, -88.5) * mm, "end": v(0, -78.2) * mm, "construction": true});
            skSolve(sketch);
        }
        {
            var Q0;
            Q0=qSketchRegion(id+"F43",true);
            extrude(context, id + "F44", {"entities" : qUnion([Q0]), "operationType" : NewBodyOperationType.REMOVE, "endBound" : BoundingType.UP_TO_NEXT, "oppositeDirection" : true, "depth" : 25 * mm});
        }
        {
            var Q0;
            {var subQ2=sQuery(id+"F35.wireOp",EDGE,"E22.bottom");var subQ3=sQuery(id+"F23.wireOp",EDGE,"E11.right");Q0=makeQuery(id+"F44.boolean.opBoolean","SPLIT",FACE,{"disambiguationData":[TD([makeQuery(id+"F24.opExtrude","SWEPT_FACE",FACE,{"disambiguationData":[OSD([subQ3])]})])],"derivedFrom":makeQuery(id+"F36.boolean.opBoolean","MERGE",FACE,{"derivedFrom":[makeQuery(id+"F24.opExtrude","CAP_FACE",FACE,{"disambiguationData":[OSD([sQuery(id+"F23.wireOp",EDGE,"E11.bottom"),sQuery(id+"F23.wireOp",EDGE,"E11.top"),sQuery(id+"F23.wireOp",EDGE,"E11.left"),subQ3])],"isStart":false}),makeQuery(id+"F36.opExtrude","SWEPT_FACE",FACE,{"disambiguationData":[OSD([subQ2])]}),makeQuery(id+"F36.opExtrude","SWEPT_FACE",FACE,{"disambiguationData":[OSD([sQuery(id+"F35.wireOp",EDGE,"E23.bottom")])]})]})});}
            var sketch = newSketch(context, id + "F45", { "sketchPlane" : qUnion([Q0])});
            skLineSegment(sketch, "E63.bottom", {"start": v(-11.4, 22.5) * mm, "end": v(11.4, 22.5) * mm});
            skLineSegment(sketch, "E63.top", {"start": v(-11.4, 20) * mm, "end": v(11.4, 20) * mm});
            skLineSegment(sketch, "E63.left", {"start": v(-11.4, 22.5) * mm, "end": v(-11.4, 20) * mm});
            skLineSegment(sketch, "E63.right", {"start": v(11.4, 22.5) * mm, "end": v(11.4, 20) * mm});
            skSolve(sketch);
        }
        {
            var Q0;
            Q0=qSketchRegion(id+"F45",true);
            extrude(context, id + "F46", {"entities" : qUnion([Q0]), "operationType" : NewBodyOperationType.ADD, "oppositeDirection" : true, "depth" : 3 * mm});
        }
        {
            var Q0;
            Q0=qCreatedBy(makeId("Front.planeOp"),FACE);
            var sketch = newSketch(context, id + "F47", { "sketchPlane" : qUnion([Q0])});
            skCircle(sketch, "E64.cCircle", {"center": v(-29.05, 0) * mm, "radius": 10 * mm, "construction": true});
            skLineSegment(sketch, "E64.0", {"start": v(-34.82, -10) * mm, "end": v(-40.6, 0) * mm});
            skLineSegment(sketch, "E64.1", {"start": v(-40.6, 0) * mm, "end": v(-34.82, 10) * mm});
            skLineSegment(sketch, "E64.2", {"start": v(-34.82, 10) * mm, "end": v(-23.28, 10) * mm});
            skLineSegment(sketch, "E64.3", {"start": v(-23.28, 10) * mm, "end": v(-17.5, 0) * mm});
            skLineSegment(sketch, "E64.4", {"start": v(-17.5, 0) * mm, "end": v(-23.28, -10) * mm});
            skLineSegment(sketch, "E64.5", {"start": v(-23.28, -10) * mm, "end": v(-34.82, -10) * mm});
            skPoint(sketch, "E64.0.midPoint", {"position": v(-37.71, -5) * mm});
            skSolve(sketch);
        }
        {
            var Q0;
            Q0=qSketchRegion(id+"F47",true);
            extrude(context, id + "F48", {"entities" : qUnion([Q0]), "oppositeDirection" : true, "depth" : 3 * mm});
        }
        {
            var Q0;
            Q0=makeQuery(id+"F48.opExtrude","CAP_FACE",FACE,{"disambiguationData":[OSD([sQuery(id+"F47.wireOp",EDGE,"E64.0"),sQuery(id+"F47.wireOp",EDGE,"E64.1"),sQuery(id+"F47.wireOp",EDGE,"E64.2"),sQuery(id+"F47.wireOp",EDGE,"E64.3"),sQuery(id+"F47.wireOp",EDGE,"E64.4"),sQuery(id+"F47.wireOp",EDGE,"E64.5")])],"isStart":false});
            var sketch = newSketch(context, id + "F49", { "sketchPlane" : qUnion([Q0])});
            skLineSegment(sketch, "E65", {"start": v(17.5, 0) * mm, "end": v(40.6, 0) * mm, "construction": true});
            skLineSegment(sketch, "E66", {"start": v(18.77, 2.2) * mm, "end": v(39.33, 2.2) * mm});
            skLineSegment(sketch, "E67.MirrorCS", {"start": v(18.77, -2.2) * mm, "end": v(39.33, -2.2) * mm});
            skLineSegment(sketch, "E68", {"start": v(18.77, 2.2) * mm, "end": v(17.5, 0) * mm});
            skLineSegment(sketch, "E69", {"start": v(17.5, 0) * mm, "end": v(18.77, -2.2) * mm});
            skLineSegment(sketch, "E70", {"start": v(39.33, -2.2) * mm, "end": v(40.6, 0) * mm});
            skLineSegment(sketch, "E71", {"start": v(40.6, 0) * mm, "end": v(39.33, 2.2) * mm});
            skSolve(sketch);
        }
        {
            var Q0;
            Q0=qCreatedBy(id+"F4.planeOp",FACE);
            var sketch = newSketch(context, id + "F50", { "sketchPlane" : qUnion([Q0])});
            skLineSegment(sketch, "E72", {"start": v(17.5, 0) * mm, "end": v(40.6, 0) * mm, "construction": true});
            skLineSegment(sketch, "E73", {"start": v(18.77, 1) * mm, "end": v(39.33, 1) * mm});
            skLineSegment(sketch, "E74", {"start": v(18.77, 3.44) * mm, "end": v(18.77, 1) * mm, "construction": true});
            skLineSegment(sketch, "E75", {"start": v(39.33, 2.62) * mm, "end": v(39.33, 1) * mm, "construction": true});
            skLineSegment(sketch, "E76.MirrorCS", {"start": v(18.77, -1) * mm, "end": v(39.33, -1) * mm});
            skLineSegment(sketch, "E77.trimOffspring", {"start": v(18.77, -1) * mm, "end": v(18.77, -3.73) * mm, "construction": true});
            skLineSegment(sketch, "E78.trimOffspring", {"start": v(39.33, -1) * mm, "end": v(39.33, -2.87) * mm, "construction": true});
            skLineSegment(sketch, "E79", {"start": v(18.77, 1) * mm, "end": v(17.5, 0) * mm});
            skLineSegment(sketch, "E80", {"start": v(18.77, -1) * mm, "end": v(17.5, 0) * mm});
            skLineSegment(sketch, "E81", {"start": v(39.33, -1) * mm, "end": v(40.6, 0) * mm});
            skLineSegment(sketch, "E82", {"start": v(40.6, 0) * mm, "end": v(39.33, 1) * mm});
            skSolve(sketch);
        }
        {
            var Q1;
            Q1=makeQuery(id+"F49.imprint","IMPRINT",FACE,{"disambiguationData":[TD([[makeQuery(id+"F49.imprint","IMPRINT",EDGE,{"derivedFrom":sQuery(id+"F49.wireOp",EDGE,"E66")}),-1.0]])]});
            var Q2;
            Q2=makeQuery(id+"F50.imprint","IMPRINT",FACE,{"disambiguationData":[TD([[makeQuery(id+"F50.imprint","IMPRINT",EDGE,{"derivedFrom":sQuery(id+"F50.wireOp",EDGE,"E73")}),-1.0]])]});
            loft(context, id + "F51", {"operationType" : NewBodyOperationType.ADD, "sheetProfilesArray" : [{ "sheetProfileEntities" : qUnion([Q1]) }, { "sheetProfileEntities" : qUnion([Q2]) }]});
        }
        {
            var Q0;
            Q0=makeQuery(id+"F51.opLoft","SWEPT_EDGE",EDGE,{"disambiguationData":[OSD([sQuery(id+"F49.wireOp",EDGE,"E68"),sQuery(id+"F49.wireOp",EDGE,"E69"),sQuery(id+"F50.wireOp",EDGE,"E79"),sQuery(id+"F50.wireOp",EDGE,"E80")])]});
            var Q1;
            Q1=makeQuery(id+"F51.opLoft","SWEPT_EDGE",EDGE,{"disambiguationData":[OSD([sQuery(id+"F47.wireOp",EDGE,"E64.4"),sQuery(id+"F49.wireOp",EDGE,"E67.MirrorCS"),sQuery(id+"F49.wireOp",EDGE,"E69"),sQuery(id+"F50.wireOp",EDGE,"E76.MirrorCS"),sQuery(id+"F50.wireOp",EDGE,"E80")])]});
            var Q2;
            Q2=makeQuery(id+"F51.opLoft","SWEPT_EDGE",EDGE,{"disambiguationData":[OSD([sQuery(id+"F47.wireOp",EDGE,"E64.3"),sQuery(id+"F49.wireOp",EDGE,"E66"),sQuery(id+"F49.wireOp",EDGE,"E68"),sQuery(id+"F50.wireOp",EDGE,"E73"),sQuery(id+"F50.wireOp",EDGE,"E79")])]});
            var Q3;
            Q3=makeQuery(id+"F51.opLoft","SWEPT_EDGE",EDGE,{"disambiguationData":[OSD([sQuery(id+"F49.wireOp",EDGE,"E70"),sQuery(id+"F49.wireOp",EDGE,"E71"),sQuery(id+"F50.wireOp",EDGE,"E81"),sQuery(id+"F50.wireOp",EDGE,"E82")])]});
            var Q4;
            Q4=makeQuery(id+"F51.opLoft","SWEPT_EDGE",EDGE,{"disambiguationData":[OSD([sQuery(id+"F47.wireOp",EDGE,"E64.0"),sQuery(id+"F49.wireOp",EDGE,"E67.MirrorCS"),sQuery(id+"F49.wireOp",EDGE,"E70"),sQuery(id+"F50.wireOp",EDGE,"E76.MirrorCS"),sQuery(id+"F50.wireOp",EDGE,"E81")])]});
            var Q5;
            Q5=makeQuery(id+"F51.opLoft","SWEPT_EDGE",EDGE,{"disambiguationData":[OSD([sQuery(id+"F47.wireOp",EDGE,"E64.1"),sQuery(id+"F49.wireOp",EDGE,"E66"),sQuery(id+"F49.wireOp",EDGE,"E71"),sQuery(id+"F50.wireOp",EDGE,"E73"),sQuery(id+"F50.wireOp",EDGE,"E82")])]});
            fillet(context, id + "F52", {"entities" : qUnion([Q0, Q1, Q2, Q3, Q4, Q5]), "radius" : 0.5 * mm, "tangentPropagation" : true, "allowEdgeOverflow" : false});
        }
        {
            var Q0;
            Q0=makeQuery(id+"F51.opLoft","MID_CAP_EDGE",EDGE,{"disambiguationData":[OSD([sQuery(id+"F47.wireOp",EDGE,"E64.1"),sQuery(id+"F47.wireOp",EDGE,"E64.3"),sQuery(id+"F49.wireOp",EDGE,"E66"),sQuery(id+"F49.wireOp",EDGE,"E68"),sQuery(id+"F49.wireOp",EDGE,"E71")])],"capPos":0.0});
            var Q1;
            Q1=makeQuery(id+"F51.opLoft","MID_CAP_EDGE",EDGE,{"disambiguationData":[OSD([sQuery(id+"F47.wireOp",EDGE,"E64.0"),sQuery(id+"F47.wireOp",EDGE,"E64.4"),sQuery(id+"F49.wireOp",EDGE,"E67.MirrorCS"),sQuery(id+"F49.wireOp",EDGE,"E69"),sQuery(id+"F49.wireOp",EDGE,"E70")])],"capPos":0.0});
            fillet(context, id + "F53", {"entities" : qUnion([Q0, Q1]), "radius" : 3 * mm, "tangentPropagation" : true, "allowEdgeOverflow" : false});
        }
        {
            var Q0;
            Q0=makeQuery(id+"F51.opLoft","MID_CAP_EDGE",EDGE,{"disambiguationData":[OSD([sQuery(id+"F50.wireOp",EDGE,"E73"),sQuery(id+"F50.wireOp",EDGE,"E79"),sQuery(id+"F50.wireOp",EDGE,"E82")])],"capPos":1.0});
            fillet(context, id + "F54", {"entities" : qUnion([Q0]), "radius" : 0.5 * mm, "tangentPropagation" : true, "allowEdgeOverflow" : false});
        }
        {
            var Q0;
            Q0=makeQuery(id+"F12.opExtrude","SWEPT_BODY",BODY,{"disambiguationData":[OSD([sQuery(id+"F11.wireOp",EDGE,"E8.bottom"),sQuery(id+"F11.wireOp",EDGE,"E8.top"),sQuery(id+"F11.wireOp",EDGE,"E8.left"),sQuery(id+"F11.wireOp",EDGE,"E8.right")])]});
            var Q1;
            Q1=makeQuery(id+"F15.opExtrude","SWEPT_BODY",BODY,{"disambiguationData":[OSD([sQuery(id+"F14.wireOp",EDGE,"E9.bottom"),sQuery(id+"F14.wireOp",EDGE,"E9.top"),sQuery(id+"F14.wireOp",EDGE,"E9.left"),sQuery(id+"F14.wireOp",EDGE,"E9.right")])]});
            deleteBodies(context, id + "F55", {"entities" : qUnion([Q0, Q1])});
        }
        {
            var Q0;
            Q0=makeQuery(id+"F48.opExtrude","SWEPT_BODY",BODY,{"disambiguationData":[OSD([sQuery(id+"F47.wireOp",EDGE,"E64.0"),sQuery(id+"F47.wireOp",EDGE,"E64.1"),sQuery(id+"F47.wireOp",EDGE,"E64.2"),sQuery(id+"F47.wireOp",EDGE,"E64.3"),sQuery(id+"F47.wireOp",EDGE,"E64.4"),sQuery(id+"F47.wireOp",EDGE,"E64.5")])]});
            deleteBodies(context, id + "F56", {"entities" : qUnion([Q0])});
        }
    });
